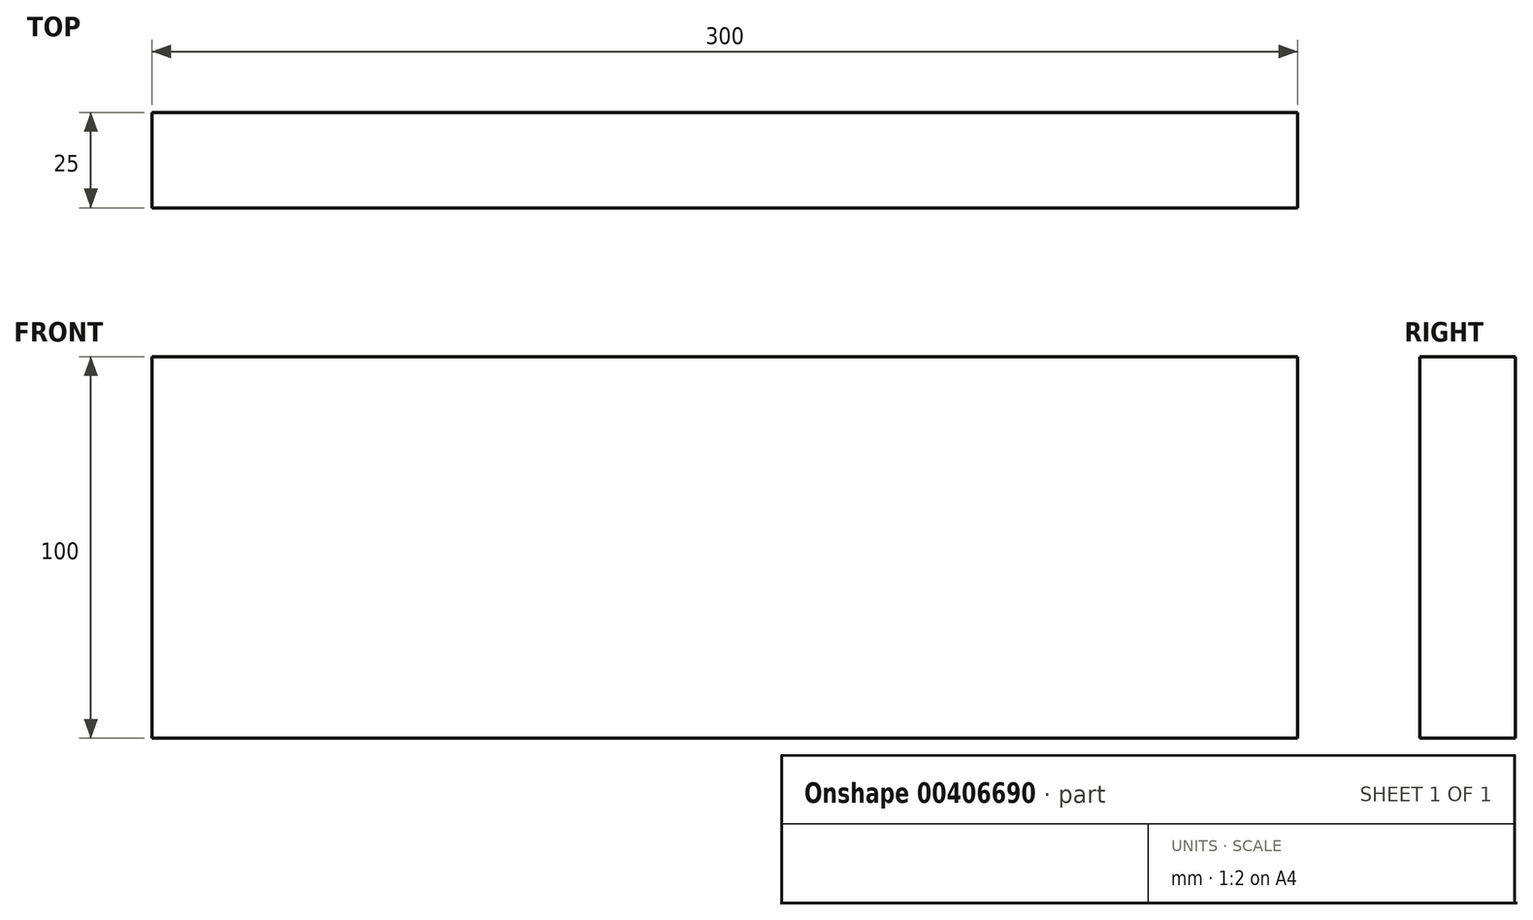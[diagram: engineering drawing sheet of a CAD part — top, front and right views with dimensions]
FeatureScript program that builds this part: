
annotation { "Feature Type Name" : "Feature", "Feature Type Description" : "" }
export const myFeature = defineFeature(function(context is Context, id is Id, definition is map)
    precondition{}
    {
        {
            var Q0;
            Q0=qCreatedBy(makeId("Front.planeOp"),FACE);
            var sketch = newSketch(context, id + "F0", { "sketchPlane" : qUnion([Q0])});
            skLineSegment(sketch, "E0", {"start": v(0, 0) * mm, "end": v(0, 100) * mm});
            skLineSegment(sketch, "E1", {"start": v(0, 100) * mm, "end": v(300, 100) * mm});
            skLineSegment(sketch, "E2", {"start": v(300, 100) * mm, "end": v(300, 0) * mm});
            skLineSegment(sketch, "E3", {"start": v(300, 0) * mm, "end": v(0, 0) * mm});
            skSolve(sketch);
        }
        {
            var Q0;
            Q0 = qSketchRegion(id + "F0", true);
            extrude(context, id + "F1", {"entities" : qUnion([Q0]), "depth" : 25 * mm});
        }
    });
